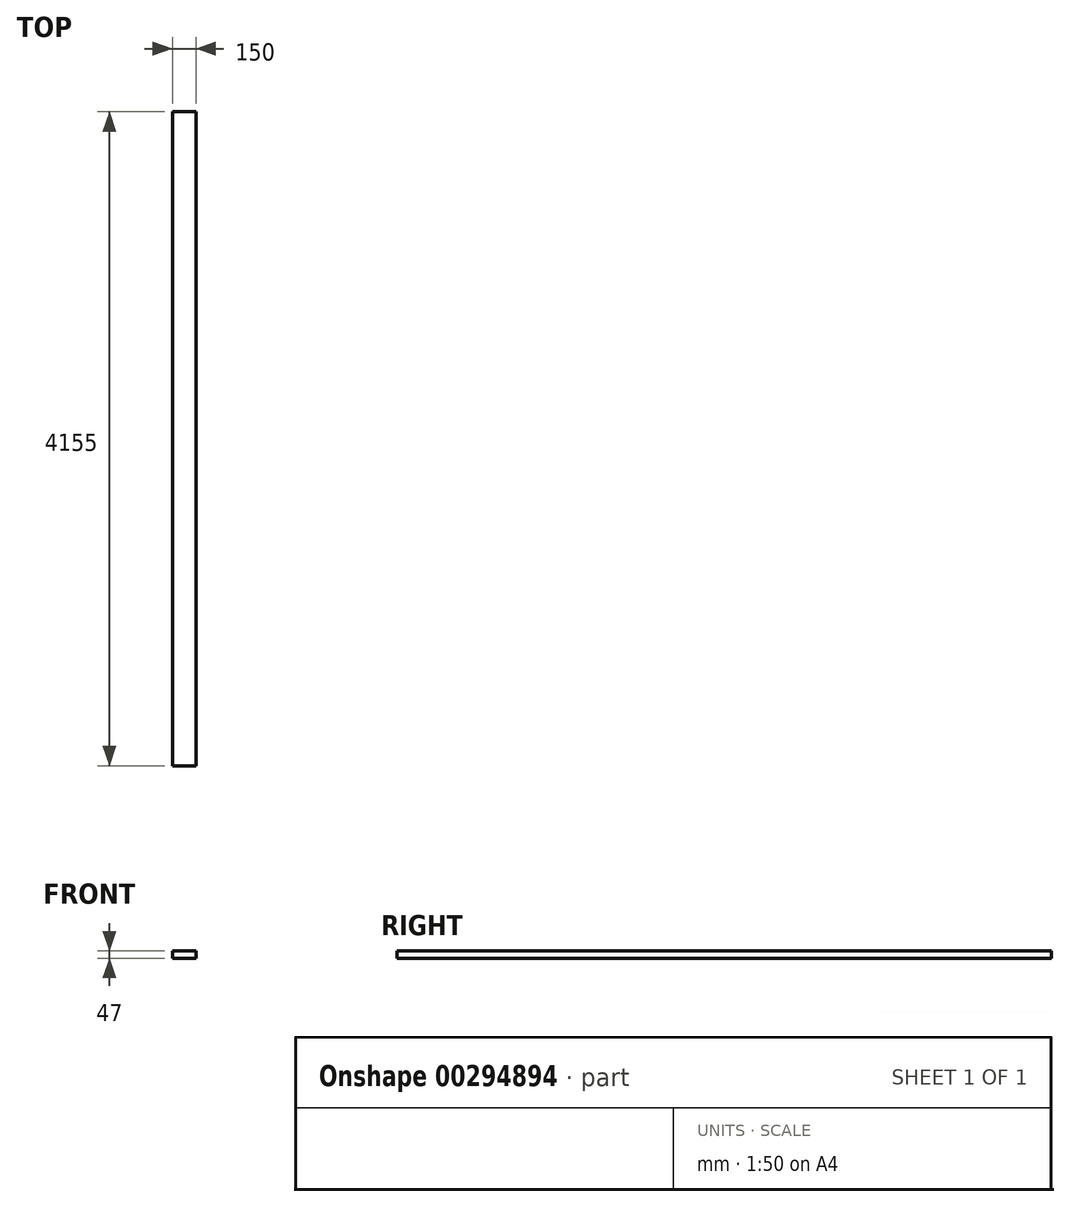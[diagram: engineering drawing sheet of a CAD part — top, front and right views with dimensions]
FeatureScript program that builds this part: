
annotation { "Feature Type Name" : "Feature", "Feature Type Description" : "" }
export const myFeature = defineFeature(function(context is Context, id is Id, definition is map)
    precondition{}
    {
        {
            var Q0;
            Q0=qCreatedBy(makeId("Front.planeOp"),FACE);
            var sketch = newSketch(context, id + "F0", { "sketchPlane" : qUnion([Q0])});
            skLineSegment(sketch, "E0.bottom", {"start": v(75, 23.5) * mm, "end": v(-75, 23.5) * mm});
            skLineSegment(sketch, "E0.top", {"start": v(75, -23.5) * mm, "end": v(-75, -23.5) * mm});
            skLineSegment(sketch, "E0.left", {"start": v(75, 23.5) * mm, "end": v(75, -23.5) * mm});
            skLineSegment(sketch, "E0.right", {"start": v(-75, 23.5) * mm, "end": v(-75, -23.5) * mm});
            skPoint(sketch, "E0.middle", {"position": v(0, 0) * mm});
            skSolve(sketch);
        }
        {
            var Q0;
            Q0 = qSketchRegion(id + "F0", true);
            extrude(context, id + "F1", {"entities" : qUnion([Q0]), "depth" : 4155 * mm});
        }
    });
